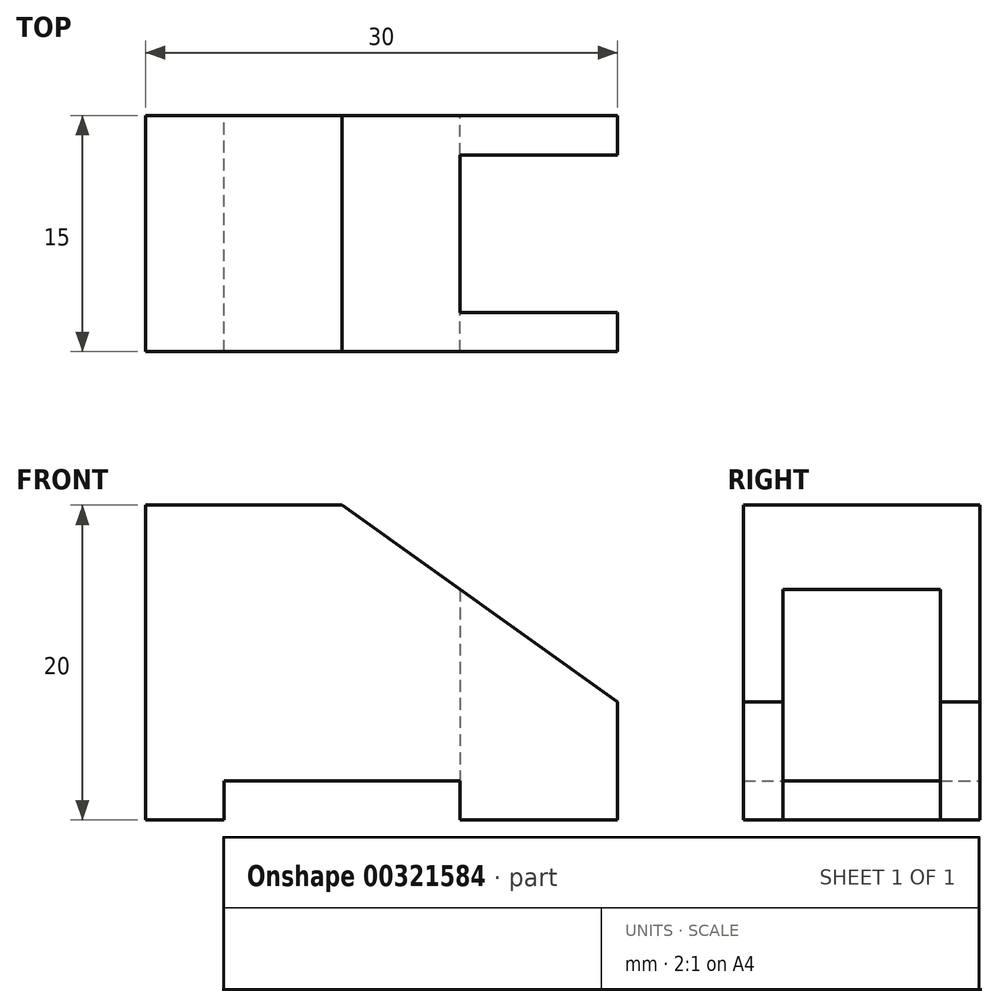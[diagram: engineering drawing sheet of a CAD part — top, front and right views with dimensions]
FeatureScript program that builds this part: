
annotation { "Feature Type Name" : "Feature", "Feature Type Description" : "" }
export const myFeature = defineFeature(function(context is Context, id is Id, definition is map)
    precondition{}
    {
        {
            var Q0;
            Q0=qCreatedBy(makeId("Front.planeOp"),FACE);
            var sketch = newSketch(context, id + "F0", { "sketchPlane" : qUnion([Q0])});
            skLineSegment(sketch, "E0", {"start": v(0, 0) * mm, "end": v(0, 20) * mm});
            skLineSegment(sketch, "E1", {"start": v(0, 20) * mm, "end": v(12.5, 20) * mm});
            skLineSegment(sketch, "E2", {"start": v(0, 0) * mm, "end": v(5, 0) * mm});
            skLineSegment(sketch, "E3", {"start": v(5, 0) * mm, "end": v(5, 2.5) * mm});
            skLineSegment(sketch, "E4", {"start": v(5, 2.5) * mm, "end": v(20, 2.5) * mm});
            skLineSegment(sketch, "E5", {"start": v(20, 2.5) * mm, "end": v(20, 0) * mm});
            skLineSegment(sketch, "E6", {"start": v(20, 0) * mm, "end": v(30, 0) * mm});
            skLineSegment(sketch, "E7", {"start": v(30, 0) * mm, "end": v(30, 7.5) * mm});
            skLineSegment(sketch, "E8", {"start": v(30, 7.5) * mm, "end": v(12.5, 20) * mm});
            skSolve(sketch);
        }
        {
            var Q0;
            Q0=makeQuery(id+"F0.imprint","IMPRINT",FACE,{"disambiguationData":[TD([[makeQuery(id+"F0.imprint","IMPRINT",EDGE,{"derivedFrom":sQuery(id+"F0.wireOp",EDGE,"E0")}),-1.0]])]});
            extrude(context, id + "F1", {"entities" : qUnion([Q0]), "depth" : 15 * mm});
        }
        {
            var Q0;
            Q0=makeQuery(id+"F1.opExtrude","SWEPT_FACE",FACE,{"disambiguationData":[OSD([sQuery(id+"F0.wireOp",EDGE,"E6")])]});
            var sketch = newSketch(context, id + "F2", { "sketchPlane" : qUnion([Q0])});
            skLineSegment(sketch, "E9", {"start": v(30, 15) * mm, "end": v(30, 12.5) * mm});
            skLineSegment(sketch, "E10", {"start": v(30, 12.5) * mm, "end": v(20, 12.5) * mm});
            skLineSegment(sketch, "E11", {"start": v(20, 12.5) * mm, "end": v(20, 2.5) * mm});
            skLineSegment(sketch, "E12", {"start": v(20, 2.5) * mm, "end": v(30, 2.5) * mm});
            skLineSegment(sketch, "E13", {"start": v(30, 2.5) * mm, "end": v(30, 12.5) * mm});
            skSolve(sketch);
        }
        {
            var Q0;
            Q0=makeQuery(id+"F2.imprint","IMPRINT",FACE,{"disambiguationData":[TD([[makeQuery(id+"F2.imprint","IMPRINT",EDGE,{"derivedFrom":sQuery(id+"F2.wireOp",EDGE,"E10")}),1.0]])]});
            extrude(context, id + "F3", {"entities" : qUnion([Q0]), "operationType" : NewBodyOperationType.REMOVE, "endBound" : BoundingType.THROUGH_ALL, "oppositeDirection" : true, "depth" : 25 * mm});
        }
    });
